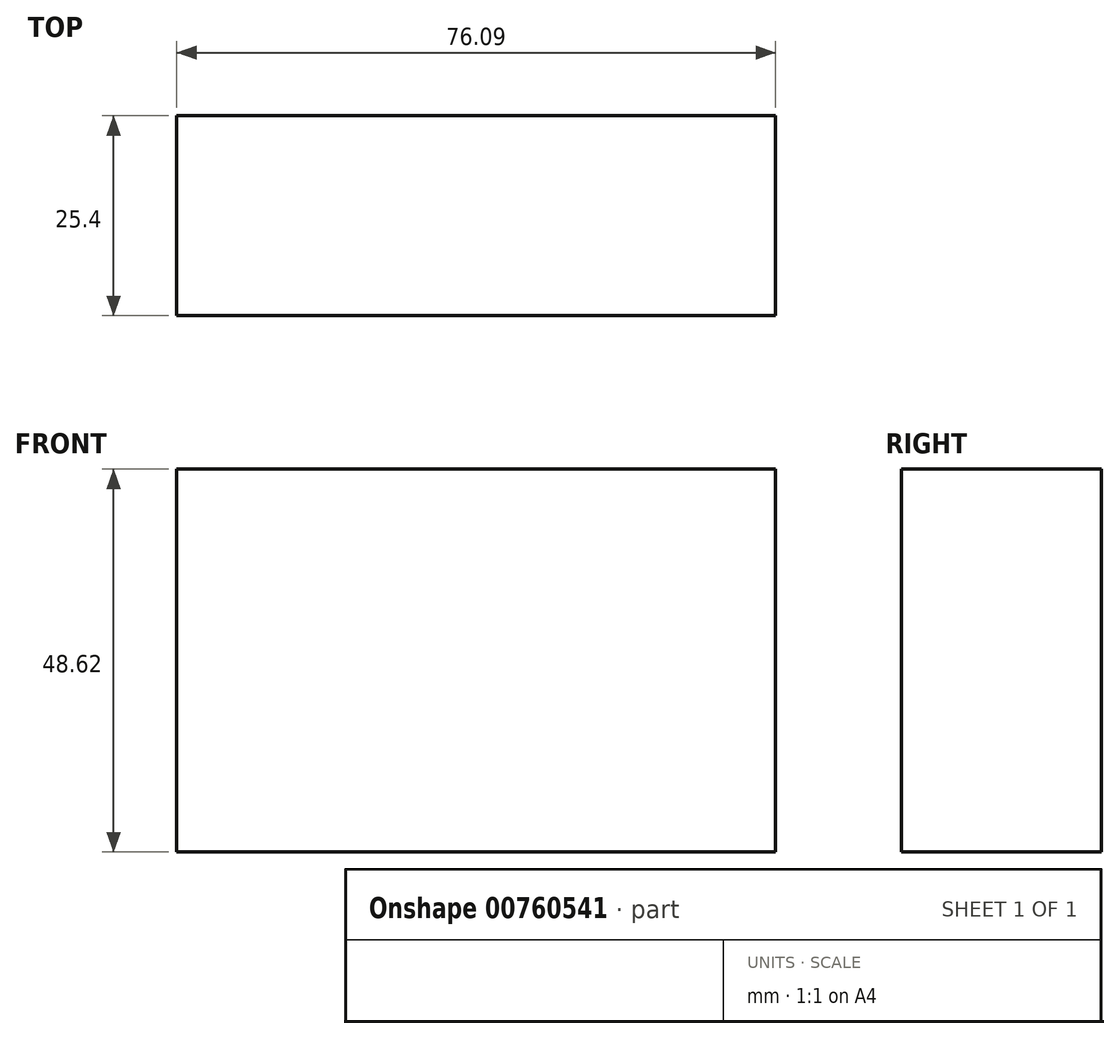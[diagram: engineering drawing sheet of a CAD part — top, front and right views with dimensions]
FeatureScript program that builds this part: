
annotation { "Feature Type Name" : "Feature", "Feature Type Description" : "" }
export const myFeature = defineFeature(function(context is Context, id is Id, definition is map)
    precondition{}
    {
        {
            var Q0;
            Q0=qCreatedBy(makeId("Front.planeOp"),FACE);
            var sketch = newSketch(context, id + "F0", { "sketchPlane" : qUnion([Q0])});
            skLineSegment(sketch, "E0.bottom", {"start": v(-39.5, 28.9) * mm, "end": v(36.59, 28.9) * mm});
            skLineSegment(sketch, "E0.top", {"start": v(-39.5, -19.71) * mm, "end": v(36.59, -19.71) * mm});
            skLineSegment(sketch, "E0.left", {"start": v(-39.5, 28.9) * mm, "end": v(-39.5, -19.71) * mm});
            skLineSegment(sketch, "E0.right", {"start": v(36.59, 28.9) * mm, "end": v(36.59, -19.71) * mm});
            skSolve(sketch);
        }
        {
            var Q0;
            Q0=makeQuery(id+"F0.imprint","IMPRINT",FACE,{"disambiguationData":[TD([[makeQuery(id+"F0.imprint","IMPRINT",EDGE,{"derivedFrom":sQuery(id+"F0.wireOp",EDGE,"E0.bottom")}),-1.0]])]});
            extrude(context, id + "F1", {"entities" : qUnion([Q0]), "depth" : 25.4 * mm, "offsetDistance" : 25.4 * mm});
        }
    });
